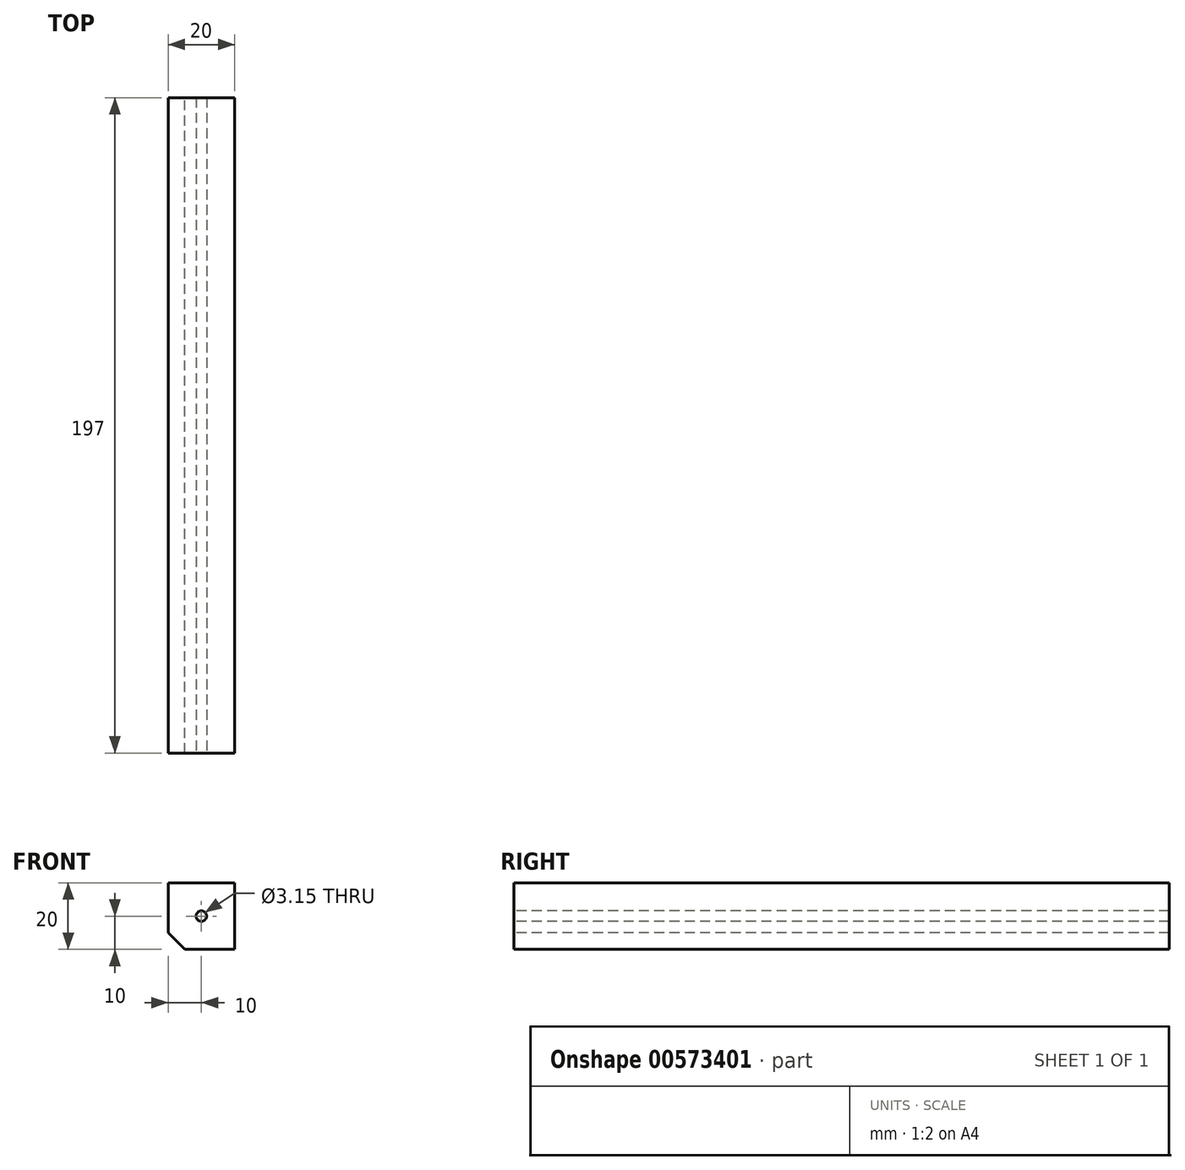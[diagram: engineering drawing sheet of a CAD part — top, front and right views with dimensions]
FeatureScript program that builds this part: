
annotation { "Feature Type Name" : "Feature", "Feature Type Description" : "" }
export const myFeature = defineFeature(function(context is Context, id is Id, definition is map)
    precondition{}
    {
        {
            var Q0;
            Q0=qCreatedBy(makeId("Front.planeOp"),FACE);
            var sketch = newSketch(context, id + "F0", { "sketchPlane" : qUnion([Q0])});
            skLineSegment(sketch, "E0.bottom", {"start": v(-10, 10) * mm, "end": v(10, 10) * mm});
            skLineSegment(sketch, "E0.top", {"start": v(-10, -10) * mm, "end": v(10, -10) * mm});
            skLineSegment(sketch, "E0.left", {"start": v(-10, 10) * mm, "end": v(-10, -10) * mm});
            skLineSegment(sketch, "E0.right", {"start": v(10, 10) * mm, "end": v(10, -10) * mm});
            skPoint(sketch, "E0.middle", {"position": v(0, 0) * mm});
            skSolve(sketch);
        }
        {
            var Q0;
            Q0 = qSketchRegion(id + "F0", true);
            extrude(context, id + "F1", {"entities" : qUnion([Q0]), "depth" : 98.5 * mm, "offsetDistance" : 25 * mm, "hasSecondDirection" : true, "secondDirectionOppositeDirection" : true, "secondDirectionDepth" : 98.5 * mm});
        }
        {
            var Q0;
            Q0=makeQuery(id+"F1.opExtrude","SWEPT_EDGE",EDGE,{"disambiguationData":[OSD([sQuery(id+"F0.wireOp",EDGE,"E0.top"),sQuery(id+"F0.wireOp",EDGE,"E0.left")])]});
            chamfer(context, id + "F2", {"entities" : qUnion([Q0]), "width" : 5 * mm, "tangentPropagation" : true});
        }
        {
            var Q0;
            Q0=makeQuery(id+"F1.opExtrude","CAP_FACE",FACE,{"disambiguationData":[OSD([sQuery(id+"F0.wireOp",EDGE,"E0.bottom"),sQuery(id+"F0.wireOp",EDGE,"E0.top"),sQuery(id+"F0.wireOp",EDGE,"E0.left"),sQuery(id+"F0.wireOp",EDGE,"E0.right")])],"isStart":false});
            var sketch = newSketch(context, id + "F3", { "sketchPlane" : qUnion([Q0])});
            skPoint(sketch, "E1", {"position": v(0, 0) * mm});
            skSolve(sketch);
        }
        {
            var Q0;
            Q0=sQuery(id+"F3.wireOp",VERTEX,"E1");
            var Q1;
            Q1=makeQuery(id+"F1.opExtrude","SWEPT_BODY",BODY,{"disambiguationData":[OSD([sQuery(id+"F0.wireOp",EDGE,"E0.bottom"),sQuery(id+"F0.wireOp",EDGE,"E0.top"),sQuery(id+"F0.wireOp",EDGE,"E0.left"),sQuery(id+"F0.wireOp",EDGE,"E0.right")])]});
            hole(context, id + "F4", {"style" : HoleStyle.SIMPLE, "endStyle" : HoleEndStyle.THROUGH, "standardTappedOrClearance" : lookupTablePath({ "standard" : "ISO", "fit" : "Close", "size" : "M3", "type" : "Clearance" }), "standardBlindInLast" : lookupTablePath({ "fit" : "Close", "standard" : "ISO", "size" : "M3", "type" : "Clearance" }), "holeDiameter" : 3.15 * mm, "majorDiameter" : 5 * mm, "isTappedThrough" : true, "tappedDepth" : 12 * mm, "tapClearance" : 3, "locations" : qUnion([Q0]), "scope" : qUnion([Q1])});
        }
    });
